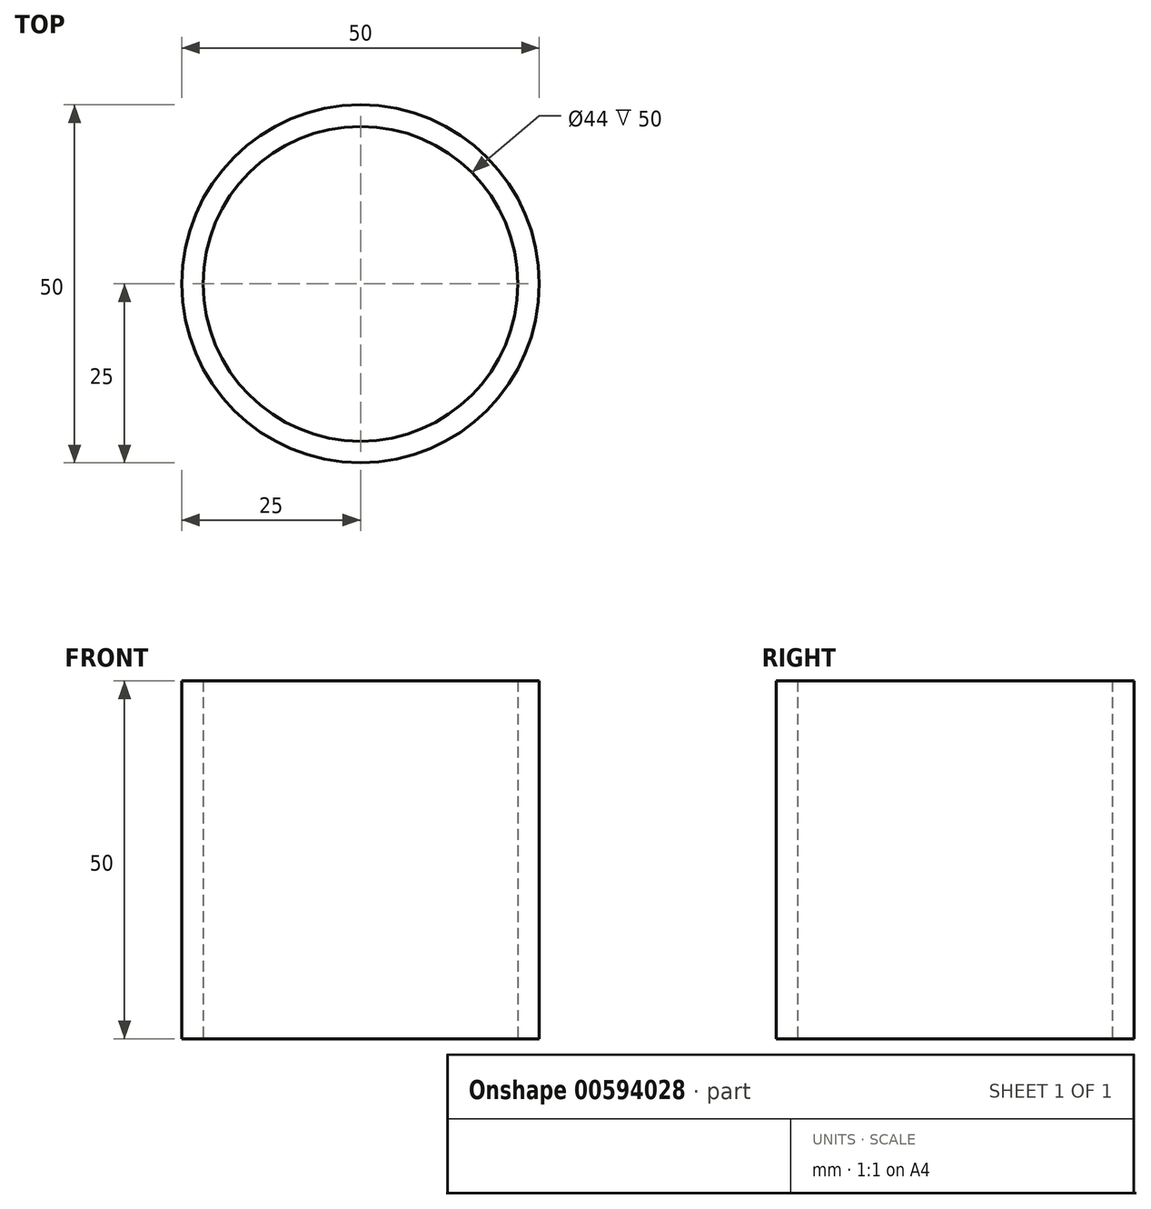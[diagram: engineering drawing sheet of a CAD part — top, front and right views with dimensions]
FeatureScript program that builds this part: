
annotation { "Feature Type Name" : "Feature", "Feature Type Description" : "" }
export const myFeature = defineFeature(function(context is Context, id is Id, definition is map)
    precondition{}
    {
        {
            var Q0;
            Q0=qCreatedBy(makeId("Top.planeOp"),FACE);
            var sketch = newSketch(context, id + "F0", { "sketchPlane" : qUnion([Q0])});
            skCircle(sketch, "E0", {"center": v(0, 0) * mm, "radius": 25 * mm});
            skCircle(sketch, "E1.0", {"center": v(0, 0) * mm, "radius": 22 * mm});
            skSolve(sketch);
        }
        {
            var Q0;
            Q0=makeQuery(id+"F0.imprint","IMPRINT",FACE,{"disambiguationData":[TD([[makeQuery(id+"F0.imprint","IMPRINT",EDGE,{"derivedFrom":sQuery(id+"F0.wireOp",EDGE,"E0")}),1.0]])]});
            extrude(context, id + "F1", {"entities" : qUnion([Q0]), "depth" : 50 * mm, "offsetDistance" : 25 * mm});
        }
    });
